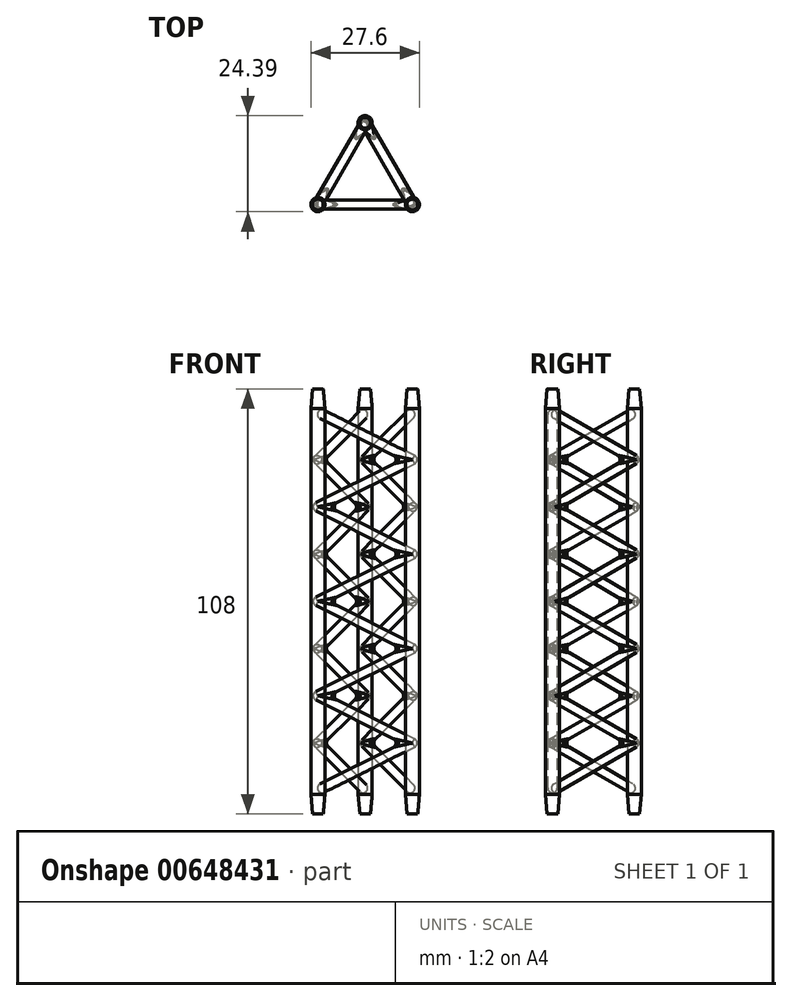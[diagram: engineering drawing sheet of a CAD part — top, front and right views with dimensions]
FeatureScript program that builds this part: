
annotation { "Feature Type Name" : "Feature", "Feature Type Description" : "" }
export const myFeature = defineFeature(function(context is Context, id is Id, definition is map)
    precondition{}
    {
        {
            var Q0;
            Q0=qCreatedBy(makeId("Top.planeOp"),FACE);
            var sketch = newSketch(context, id + "F0", { "sketchPlane" : qUnion([Q0])});
            skLineSegment(sketch, "E0", {"start": v(-12, -6.93) * mm, "end": v(12, -6.93) * mm});
            skLineSegment(sketch, "E1", {"start": v(12, -6.93) * mm, "end": v(0, 13.86) * mm});
            skLineSegment(sketch, "E2", {"start": v(0, 13.86) * mm, "end": v(-12, -6.93) * mm});
            skLineSegment(sketch, "E3", {"start": v(-6, 3.46) * mm, "end": v(12, -6.93) * mm});
            skLineSegment(sketch, "E4", {"start": v(6, 3.46) * mm, "end": v(-12, -6.93) * mm});
            skLineSegment(sketch, "E5", {"start": v(0, 13.86) * mm, "end": v(0, -6.93) * mm});
            skSolve(sketch);
        }
        {
            var Q0;
            Q0=qCreatedBy(makeId("Front.planeOp"),FACE);
            var sketch = newSketch(context, id + "F1", { "sketchPlane" : qUnion([Q0])});
            skLineSegment(sketch, "E6", {"start": v(0, 0) * mm, "end": v(0, 15.44) * mm});
            skSolve(sketch);
        }
        {
            var Q0;
            Q0=qCreatedBy(makeId("Top.planeOp"),FACE);
            var sketch = newSketch(context, id + "F2", { "sketchPlane" : qUnion([Q0])});
            skCircle(sketch, "E7", {"center": v(-12, -6.93) * mm, "radius": 1.8 * mm});
            skSolve(sketch);
        }
        {
            var Q0;
            Q0=makeQuery(id+"F2.imprint","IMPRINT",FACE,{"disambiguationData":[TD([[makeQuery(id+"F2.imprint","IMPRINT",EDGE,{"derivedFrom":sQuery(id+"F2.wireOp",EDGE,"E7")}),1.0]])]});
            var Q1;
            Q1=sQuery(id+"F2.wireOp",EDGE,"E7");
            extrude(context, id + "F3", {"entities" : qUnion([Q0]), "surfaceEntities" : qUnion([Q1]), "depth" : 102 * mm, "offsetDistance" : 25 * mm, "hasSecondDirection" : true, "secondDirectionOppositeDirection" : true, "secondDirectionDepth" : 6 * mm});
        }
        {
            var Q0;
            Q0=sQuery(id+"F0.wireOp",EDGE,"E0");
            var Q1;
            Q1=sQuery(id+"F1.wireOp",EDGE,"E6");
            cPlane(context, id + "F4", {"entities" : qUnion([Q0, Q1]), "cplaneType" : CPlaneType.LINE_ANGLE, "offset" : 25 * mm, "angle" : 0 * degree, "width" : 150 * mm, "height" : 150 * mm});
        }
        {
            var Q0;
            Q0=qCreatedBy(id+"F4.planeOp",FACE);
            var sketch = newSketch(context, id + "F5", { "sketchPlane" : qUnion([Q0])});
            skLineSegment(sketch, "E8", {"start": v(-12, 0) * mm, "end": v(12, 12) * mm});
            skLineSegment(sketch, "E9", {"start": v(12, 12) * mm, "end": v(12, 0) * mm, "construction": true});
            skLineSegment(sketch, "E10", {"start": v(-12, 0) * mm, "end": v(-12, 24) * mm, "construction": true});
            skLineSegment(sketch, "E11", {"start": v(-12, 24) * mm, "end": v(12, 12) * mm});
            skLineSegment(sketch, "E12", {"start": v(-12, 24) * mm, "end": v(12, 36) * mm});
            skLineSegment(sketch, "E13", {"start": v(12, 36) * mm, "end": v(-12, 48) * mm});
            skLineSegment(sketch, "E14", {"start": v(-12, 48) * mm, "end": v(12, 60) * mm});
            skLineSegment(sketch, "E15", {"start": v(12, 60) * mm, "end": v(-12, 72) * mm});
            skLineSegment(sketch, "E16", {"start": v(-12, 72) * mm, "end": v(12, 84) * mm});
            skLineSegment(sketch, "E17", {"start": v(12, 84) * mm, "end": v(-12, 96) * mm});
            skLineSegment(sketch, "E18", {"start": v(-12, 96) * mm, "end": v(-12, 72) * mm, "construction": true});
            skLineSegment(sketch, "E19", {"start": v(-12, 48) * mm, "end": v(-12, 24) * mm, "construction": true});
            skLineSegment(sketch, "E20", {"start": v(-12, 48) * mm, "end": v(-12, 72) * mm, "construction": true});
            skLineSegment(sketch, "E21", {"start": v(12, 12) * mm, "end": v(12, 36) * mm, "construction": true});
            skLineSegment(sketch, "E22", {"start": v(12, 36) * mm, "end": v(12, 60) * mm, "construction": true});
            skLineSegment(sketch, "E23", {"start": v(12, 60) * mm, "end": v(12, 84) * mm, "construction": true});
            skLineSegment(sketch, "E24", {"start": v(-12, 96) * mm, "end": v(12, 108) * mm});
            skLineSegment(sketch, "E25", {"start": v(12, 108) * mm, "end": v(12, 84) * mm, "construction": true});
            skLineSegment(sketch, "E26", {"start": v(-12.25, 120) * mm, "end": v(12, 108) * mm});
            skLineSegment(sketch, "E27", {"start": v(-12.25, 120) * mm, "end": v(-12, 96) * mm, "construction": true});
            skLineSegment(sketch, "E28", {"start": v(12, 0) * mm, "end": v(-12, 0) * mm});
            skLineSegment(sketch, "E29", {"start": v(12, 108) * mm, "end": v(12, 132) * mm, "construction": true});
            skLineSegment(sketch, "E30", {"start": v(12, 132) * mm, "end": v(-12.25, 120) * mm});
            skLineSegment(sketch, "E31", {"start": v(-12.25, 120) * mm, "end": v(-12.25, 144) * mm, "construction": true});
            skLineSegment(sketch, "E32", {"start": v(12, 132) * mm, "end": v(-12.25, 144) * mm});
            skLineSegment(sketch, "E33", {"start": v(12, 144) * mm, "end": v(-12.25, 144) * mm});
            skLineSegment(sketch, "E34", {"start": v(12, 132) * mm, "end": v(12, 144) * mm, "construction": true});
            skSolve(sketch);
        }
        {
            var Q0;
            Q0=sQuery(id+"F0.wireOp",VERTEX,"E4.end");
            var Q1;
            Q1=sQuery(id+"F5.wireOp",EDGE,"E8");
            cPlane(context, id + "F6", {"entities" : qUnion([Q0, Q1]), "cplaneType" : CPlaneType.LINE_POINT, "offset" : 25 * mm, "width" : 150 * mm, "height" : 150 * mm});
        }
        {
            var Q0;
            Q0=qCreatedBy(id+"F6.planeOp",FACE);
            var sketch = newSketch(context, id + "F7", { "sketchPlane" : qUnion([Q0])});
            skCircle(sketch, "E35", {"center": v(-6.93, 5.37) * mm, "radius": 1.2 * mm});
            skSolve(sketch);
        }
        {
            var Q0;
            Q0=makeQuery(id+"F7.imprint","IMPRINT",FACE,{"disambiguationData":[TD([[makeQuery(id+"F7.imprint","IMPRINT",EDGE,{"derivedFrom":sQuery(id+"F7.wireOp",EDGE,"E35")}),1.0]])]});
            var Q1;
            Q1=sQuery(id+"F5.wireOp",EDGE,"E8");
            var Q2;
            Q2=sQuery(id+"F5.wireOp",EDGE,"E11");
            var Q3;
            Q3=sQuery(id+"F5.wireOp",EDGE,"E12");
            var Q4;
            Q4=sQuery(id+"F5.wireOp",EDGE,"E13");
            var Q5;
            Q5=sQuery(id+"F5.wireOp",EDGE,"E14");
            var Q6;
            Q6=sQuery(id+"F5.wireOp",EDGE,"E15");
            var Q7;
            Q7=sQuery(id+"F5.wireOp",EDGE,"E16");
            var Q8;
            Q8=sQuery(id+"F5.wireOp",EDGE,"E17");
            sweep(context, id + "F8", {"profiles" : qUnion([Q0]), "path" : qUnion([Q1, Q2, Q3, Q4, Q5, Q6, Q7, Q8])});
        }
        {
            var Q0;
            Q0=makeQuery(id+"F8.opSweep","SWEPT_FACE",FACE,{"disambiguationData":[OSD([sQuery(id+"F5.wireOp",EDGE,"E8"),sQuery(id+"F7.wireOp",EDGE,"E35")])]});
            var Q1;
            Q1=makeQuery(id+"F8.opSweep","SWEPT_FACE",FACE,{"disambiguationData":[OSD([sQuery(id+"F5.wireOp",EDGE,"E11"),sQuery(id+"F7.wireOp",EDGE,"E35")])]});
            var Q2;
            Q2=makeQuery(id+"F8.opSweep","SWEPT_FACE",FACE,{"disambiguationData":[OSD([sQuery(id+"F5.wireOp",EDGE,"E12"),sQuery(id+"F7.wireOp",EDGE,"E35")])]});
            var Q3;
            Q3=makeQuery(id+"F8.opSweep","SWEPT_FACE",FACE,{"disambiguationData":[OSD([sQuery(id+"F5.wireOp",EDGE,"E13"),sQuery(id+"F7.wireOp",EDGE,"E35")])]});
            var Q4;
            Q4=makeQuery(id+"F8.opSweep","SWEPT_FACE",FACE,{"disambiguationData":[OSD([sQuery(id+"F5.wireOp",EDGE,"E16"),sQuery(id+"F7.wireOp",EDGE,"E35")])]});
            var Q5;
            Q5=makeQuery(id+"F8.opSweep","SWEPT_FACE",FACE,{"disambiguationData":[OSD([sQuery(id+"F5.wireOp",EDGE,"E24"),sQuery(id+"F7.wireOp",EDGE,"E35")])]});
            var Q6;
            Q6=makeQuery(id+"F8.opSweep","SWEPT_FACE",FACE,{"disambiguationData":[OSD([sQuery(id+"F5.wireOp",EDGE,"E26"),sQuery(id+"F7.wireOp",EDGE,"E35")])]});
            var Q7;
            Q7=makeQuery(id+"F8.opSweep","SWEPT_FACE",FACE,{"disambiguationData":[OSD([sQuery(id+"F5.wireOp",EDGE,"E15"),sQuery(id+"F7.wireOp",EDGE,"E35")])]});
            var Q8;
            Q8=makeQuery(id+"F8.opSweep","SWEPT_FACE",FACE,{"disambiguationData":[OSD([sQuery(id+"F5.wireOp",EDGE,"E14"),sQuery(id+"F7.wireOp",EDGE,"E35")])]});
            var Q9;
            Q9=makeQuery(id+"F8.opSweep","SWEPT_FACE",FACE,{"disambiguationData":[OSD([sQuery(id+"F5.wireOp",EDGE,"E17"),sQuery(id+"F7.wireOp",EDGE,"E35")])]});
            var Q10;
            Q10=makeQuery(id+"F8.opSweep","MID_CAP_EDGE",EDGE,{"disambiguationData":[OSD([sQuery(id+"F5.wireOp",VERTEX,"E32.start"),sQuery(id+"F7.wireOp",EDGE,"E35")])],"capPos":12.0});
            var Q11;
            Q11=makeQuery(id+"F8.opSweep","MID_CAP_EDGE",EDGE,{"disambiguationData":[OSD([sQuery(id+"F5.wireOp",VERTEX,"E33.end"),sQuery(id+"F7.wireOp",EDGE,"E35")])],"capPos":13.0});
            fillet(context, id + "F9", {"entities" : qUnion([Q0, Q1, Q2, Q3, Q4, Q5, Q6, Q7, Q8, Q9, Q10, Q11]), "radius" : 1.2 * mm, "tangentPropagation" : true, "allowEdgeOverflow" : false});
        }
        {
            var Q0;
            Q0=makeQuery(id+"FOFZZQhrRr9CB2q_1.opPattern","COPY",BODY,{"derivedFrom":makeQuery(id+"FBj1d7q4FQKIzEE_0.opExtrude","SWEPT_BODY",BODY,{"disambiguationData":[OSD([sQuery(id+"FcsWX7URlHym1KC_0.wireOp",EDGE,"24a714e4-7966-4e9e-99a7-43efdcecc9a9")])]}),"instanceName":"1"});
            var Q1;
            Q1=makeQuery(id+"FBj1d7q4FQKIzEE_0.opExtrude","SWEPT_BODY",BODY,{"disambiguationData":[OSD([sQuery(id+"FcsWX7URlHym1KC_0.wireOp",EDGE,"24a714e4-7966-4e9e-99a7-43efdcecc9a9")])]});
            var Q2;
            Q2=makeQuery(id+"F3.opExtrude","SWEPT_BODY",BODY,{"disambiguationData":[OSD([sQuery(id+"F2.wireOp",EDGE,"E7")])]});
            var Q3;
            Q3=makeQuery(id+"F8.opSweep","SWEPT_BODY",BODY,{"disambiguationData":[OSD([sQuery(id+"F5.wireOp",EDGE,"E26"),sQuery(id+"F7.wireOp",EDGE,"E35")])]});
            var Q4;
            Q4=sQuery(id+"F1.wireOp",EDGE,"E6");
            circularPattern(context, id + "F10", {"entities" : qUnion([Q0, Q1, Q2, Q3]), "axis" : qUnion([Q4]), "angle" : 360 * degree, "instanceCount" : 3, "equalSpace" : true});
        }
        {
            var Q0;
            Q0=makeQuery(id+"F3.opExtrude","CAP_EDGE",EDGE,{"disambiguationData":[OSD([sQuery(id+"F2.wireOp",EDGE,"E7")])],"isStart":true});
            var Q1;
            Q1=makeQuery(id+"F10.opPattern","COPY",EDGE,{"derivedFrom":makeQuery(id+"F3.opExtrude","CAP_EDGE",EDGE,{"disambiguationData":[OSD([sQuery(id+"F2.wireOp",EDGE,"E7")])],"isStart":true}),"instanceName":"1"});
            var Q2;
            Q2=makeQuery(id+"F10.opPattern","COPY",EDGE,{"derivedFrom":makeQuery(id+"F3.opExtrude","CAP_EDGE",EDGE,{"disambiguationData":[OSD([sQuery(id+"F2.wireOp",EDGE,"E7")])],"isStart":true}),"instanceName":"2"});
            chamfer(context, id + "F11", {"entities" : qUnion([Q0, Q1, Q2]), "chamferType" : ChamferType.OFFSET_ANGLE, "width" : 5 * mm, "oppositeDirection" : false, "angle" : 5 * degree, "tangentPropagation" : true});
        }
        {
            var Q0;
            Q0=makeQuery(id+"F10.opPattern","COPY",EDGE,{"derivedFrom":makeQuery(id+"F3.opExtrude","CAP_EDGE",EDGE,{"disambiguationData":[OSD([sQuery(id+"F2.wireOp",EDGE,"E7")])],"isStart":false}),"instanceName":"1"});
            var Q1;
            Q1=makeQuery(id+"F10.opPattern","COPY",EDGE,{"derivedFrom":makeQuery(id+"F3.opExtrude","CAP_EDGE",EDGE,{"disambiguationData":[OSD([sQuery(id+"F2.wireOp",EDGE,"E7")])],"isStart":false}),"instanceName":"2"});
            var Q2;
            Q2=makeQuery(id+"F3.opExtrude","CAP_EDGE",EDGE,{"disambiguationData":[OSD([sQuery(id+"F2.wireOp",EDGE,"E7")])],"isStart":false});
            chamfer(context, id + "F12", {"entities" : qUnion([Q0, Q1, Q2]), "chamferType" : ChamferType.OFFSET_ANGLE, "width" : 5 * mm, "oppositeDirection" : true, "angle" : 5 * degree, "tangentPropagation" : true});
        }
    });
